# Revit family: OKA-G Kanaleinheit für GESR9, Höhe 40-240mm
name_source: partatom
category: Generic Models
revit_build: Autodesk Revit 2015 (Build: 20140606_1530(x64)
units: mm (PartAtom-declared; Revit-internal decimal feet)

## types (3) — shared parameters
Cut's number = 3
Manufacturer = OBO Bettermann
Material = Steel, Galvanized
URL = http://www.obo-bettermann.com

## per-type parameters (varying)
| type | Article Type | GTIN | Manufacturer Art. No. | Width |
| OKA-G40040240DR9 | OKA-G40040240DR9 | 4012195243762 | 7424260

7424260

7424260

7424260

7424260

7424260

7424260
7424260 | 400 mm  [stored 1.31234 ft] |
| OKA-G50040240DR9 | OKA-G50040240DR9 | 4012195243779 | 7424262 | 500 mm  [stored 1.64042 ft] |
| OKA-G60040240DR9 | OKA-G60040240DR9

OKA-G60040240DR9
OKA-G60040240DR9 | 4012195243786

4012195243700
4012195243700 | 7424264 | 600 mm |

note: [stored X ft] marks values corroborated as IEEE doubles in the binary element streams (Revit-internal decimal feet)

## geometry (parser evidence)
native form markers: Sweep x2
no freeform markers — native parametric forms only
